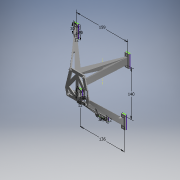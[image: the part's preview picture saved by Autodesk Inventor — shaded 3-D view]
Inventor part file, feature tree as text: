
AUTODESK INVENTOR PART (.ipt)
format: ipt  version: 2019 (Build 230136000, 136)  size: 1,030,656 bytes
history: native  units: mm (DEFAULTED — no unit token found)
features: other x19, extrude x15, loft x9, sketch x6, hole x2, chamfer x2, projected_geometry x1
ambient origin geometry x8: Origin, YZ Plane, XZ Plane, XY Plane, X Axis, Y Axis, Z Axis, Center Point
bodies: Solid1 (feature_tree)
feature tree (54):
  sketch  "Sketch1"  dims[d0=40.0mm d1=42.0mm]
  extrude  "Extrusion1"  Depth=42.0mm
  extrude  "Extrusion2"  Depth=56.0mm
  other  "deck_plate"
  sketch  "Sketch2"  dims[d2=28.0mm d3=56.0mm]
  extrude  "Extrusion3"  Depth=3.0mm
  extrude  "Extrusion4"  Depth=3.0mm
  extrude  "Extrusion5"  Depth=74.0mm
  loft  "Loft1"
  extrude  "Extrusion6"  Depth=8.0mm
  extrude  "Extrusion7"  Depth=9.0mm
  loft  "Loft2"
  loft  "Loft3"
  extrude  "Extrusion8"  Depth=8.0mm
  loft  "Loft4"
  loft  "Loft5"
  extrude  "Extrusion9"  Depth=8.5mm
  extrude  "Extrusion10"  Depth=8.5mm
  extrude  "Extrusion11"  Depth=20.0mm
  loft  "Loft6"
  loft  "Loft7"
  extrude  "Extrusion12"  Depth=10.0mm
  loft  "Loft8"
  loft  "Loft9"
  hole  "Hole1"  [1 undecoded]
  hole  "Hole2"  [1 undecoded]
  extrude  "Extrusion13"  Depth=8.5mm
  sketch  "Sketch6"  dims[d11=63.0mm d12=2.5mm d13=8.0mm d14=9.0mm d15=4.0mm d16=8.0mm d17=8.0mm d18=12.0mm d19=8.5mm d20=8.5mm d21=8.5mm d26=20.0mm d27=5.0mm d30=5.0mm d31=10.0mm d32=5.0mm d33=15.0mm d35=10.0mm d36=5.0mm d37=0.0mm d38=8.5mm d39=23.5mm d40=10.0mm d41=5.0mm d42=2.0mm d43=0.0mm d44=-75.0mm d45=3.0mm d46=27.0mm d47=37.5mm d48=20.0mm d49=5.0mm d50=12.0mm d51=3.5mm d52=0.0mm d53=3.6mm d54=0.0mm d55=0.1mm d56=0.0mm d57=0.0mm d58=90.0deg d59=0.0mm d60=90.0deg d61=3.0mm d62=3.0mm d63=30.0mm d64=12.0mm d65=40.0mm d66=5.0mm d67=20.0mm d68=136.0mm d69=4.5mm d70=3.5mm d71=0.0mm d72=3.6mm d73=0.0mm d74=0.0mm d75=90.0deg d76=0.0mm d77=90.0deg d78=0.0mm d79=90.0deg d80=0.0mm d81=90.0deg d82=0.1mm d83=0.0mm d84=0.0mm d85=90.0deg d86=0.0mm d87=90.0deg d88=0.0mm d89=90.0deg d90=0.0mm d91=90.0deg d92=3.0mm d93=3.0mm d94=30.0mm d95=12.0mm d96=40.0mm d97=5.0mm d98=20.0mm d99=159.0mm d100=140.0mm d101=5.0mm d102=15.0mm d103=10.0mm d104=0.1mm d105=0.0mm d106=3.5mm d107=0.0mm d108=3.6mm d109=0.0mm d110=0.0mm d111=90.0deg d112=0.0mm d113=90.0deg d114=0.0mm d115=90.0deg d116=0.0mm d117=90.0deg d118=5.0mm d119=20.0mm d120=10.0mm d121=0.1mm d122=0.0mm d123=0.0mm d124=90.0deg d125=0.0mm d126=90.0deg d127=0.0mm d128=90.0deg d129=0.0mm d130=90.0deg d131=6.0mm d132=6.0mm d133=4.0mm d134=2.0mm d135=90.0deg d136=8.0mm d137=20.594885mm d138=3.2mm d139=6.0mm d140=4.0mm d141=2.0mm d142=90.0deg d143=8.0mm d144=20.594885mm d148=1.0mm d149=0.0mm d150=21.0mm d151=6.0mm d152=3.0mm d153=3.0mm d154=3.0mm d155=3.0mm d156=4.25mm d157=0.0mm d158=3.0mm d159=0.0mm d160=1.75mm d161=4.0mm d162=45.0deg d163=23.0mm d164=4.0mm d165=45.0deg]
  extrude  "Extrusion14"  Depth=23.5mm
  extrude  "Extrusion15"  Depth=10.0mm
  chamfer  "Chamfer1"  Distance=5.0mm
  chamfer  "Chamfer2"  Distance=2.0mm
  other  "Edges1"
  other  "Edges2"
  other  "Edges3"
  other  "Edges4"
  other  "Edges5"
  other  "Edges6"
  other  "Edges7"
  other  "Edges8"
  other  "Edges9"
  other  "Edges10"
  other  "Edges11"
  other  "Edges12"
  other  "Edges13"
  other  "Edges14"
  other  "Edges15"
  other  "Edges16"
  other  "Edges17"
  other  "Edges18"
  sketch  "Sketch3"  dims[d5=3.0mm d6=3.0mm]
  sketch  "Sketch4"  dims[d7=3.0mm d8=3.0mm]
  sketch  "Sketch5"  dims[d9=45.0mm d10=74.0mm]
  projected_geometry  "Projected Loop1"
note: 2 required parameter values undecoded (feature->parameter linkage not recoverable at this tier; creation-order binding heuristic only, values carry confidence <= 0.55)
